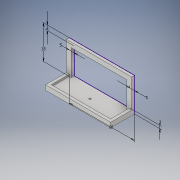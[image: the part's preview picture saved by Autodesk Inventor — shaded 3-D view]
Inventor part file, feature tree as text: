
AUTODESK INVENTOR PART (.ipt)
format: ipt  version: 2019 (Build 230136000, 136)  size: 138,752 bytes
history: native  units: mm
features: extrude x4, sketch x3, other x1
ambient origin geometry x8: Origin, YZ Plane, XZ Plane, XY Plane, X Axis, Y Axis, Z Axis, Center Point
bodies: Body1 (feature_tree)
feature tree (8):
  other  "Твердое тело1"
  sketch  "Эскиз1"
  extrude  "Выдавливание1"  Depth=5.0mm
  extrude  "Выдавливание2"  Depth=5.0mm
  extrude  "Выдавливание3"  Depth=5.0mm
  extrude  "Выдавливание4"  Depth=3.0mm
  sketch  "Эскиз2"
  sketch  "Эскиз3"
